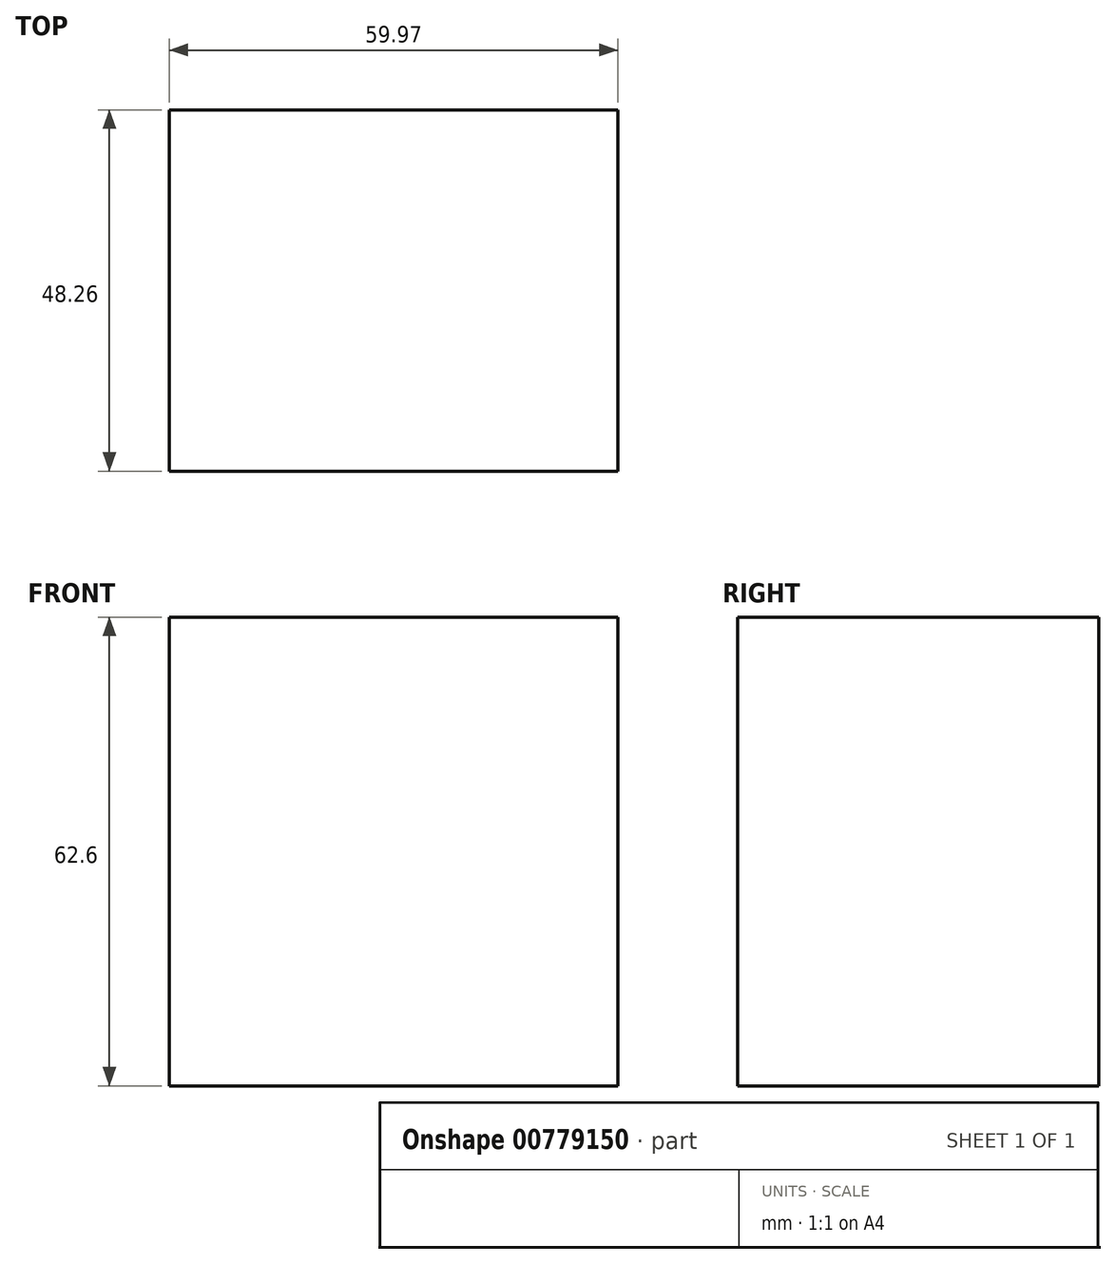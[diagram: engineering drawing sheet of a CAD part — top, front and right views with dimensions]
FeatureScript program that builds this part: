
annotation { "Feature Type Name" : "Feature", "Feature Type Description" : "" }
export const myFeature = defineFeature(function(context is Context, id is Id, definition is map)
    precondition{}
    {
        {
            var Q0;
            Q0=qCreatedBy(makeId("Front.planeOp"),FACE);
            var sketch = newSketch(context, id + "F0", { "sketchPlane" : qUnion([Q0])});
            skLineSegment(sketch, "E0.bottom", {"start": v(0, 0) * mm, "end": v(59.97, 0) * mm});
            skLineSegment(sketch, "E0.top", {"start": v(0, 62.6) * mm, "end": v(59.97, 62.6) * mm});
            skLineSegment(sketch, "E0.left", {"start": v(0, 0) * mm, "end": v(0, 62.6) * mm});
            skLineSegment(sketch, "E0.right", {"start": v(59.97, 0) * mm, "end": v(59.97, 62.6) * mm});
            skSolve(sketch);
        }
        {
            var Q0;
            Q0=makeQuery(id+"F0.imprint","IMPRINT",FACE,{"disambiguationData":[TD([[makeQuery(id+"F0.imprint","IMPRINT",EDGE,{"derivedFrom":sQuery(id+"F0.wireOp",EDGE,"E0.bottom")}),1.0]])]});
            extrude(context, id + "F1", {"entities" : qUnion([Q0]), "depth" : 48.26 * mm, "offsetDistance" : 25.4 * mm});
        }
    });
